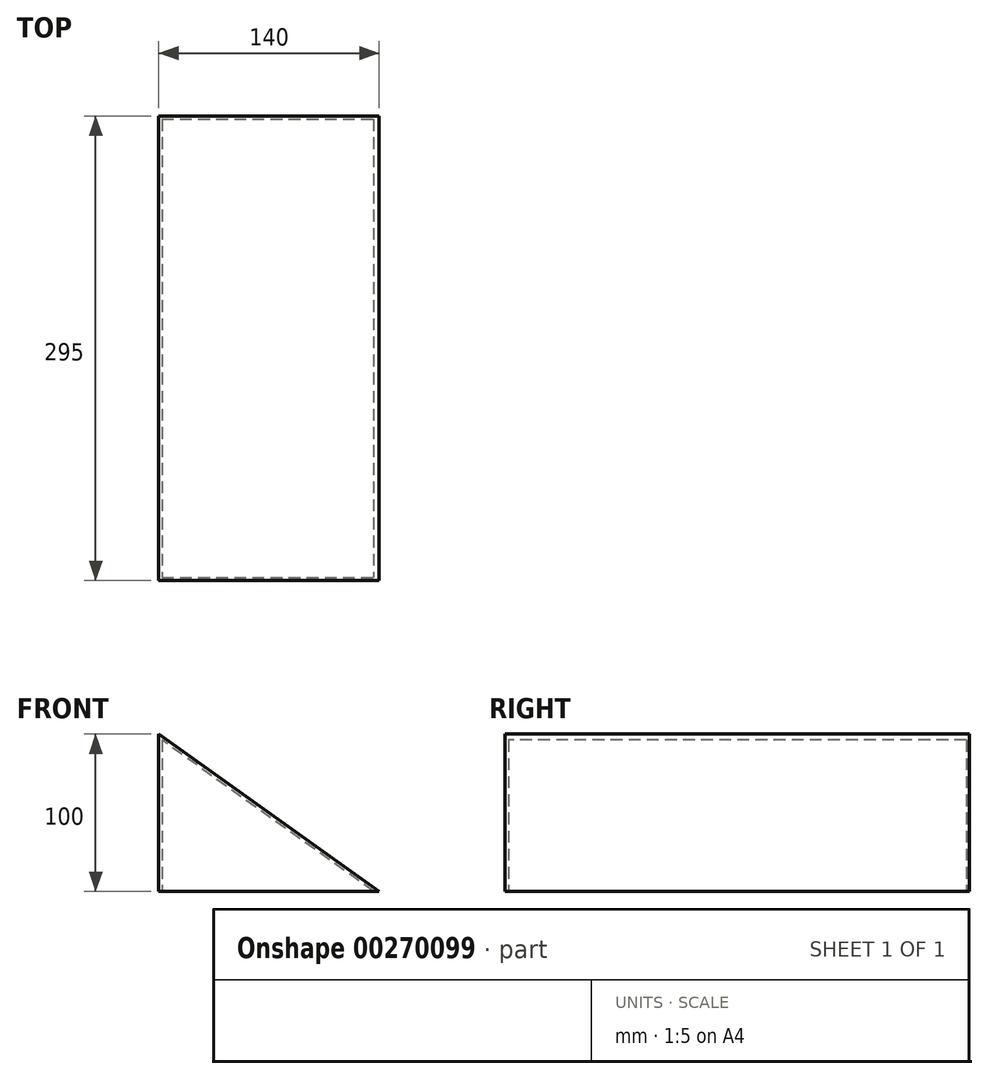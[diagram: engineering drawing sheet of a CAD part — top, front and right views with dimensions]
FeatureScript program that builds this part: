
annotation { "Feature Type Name" : "Feature", "Feature Type Description" : "" }
export const myFeature = defineFeature(function(context is Context, id is Id, definition is map)
    precondition{}
    {
        {
            var Q0;
            Q0=qCreatedBy(makeId("Front.planeOp"),FACE);
            var sketch = newSketch(context, id + "F0", { "sketchPlane" : qUnion([Q0])});
            skLineSegment(sketch, "E0", {"start": v(-70, 0) * mm, "end": v(70, 0) * mm});
            skLineSegment(sketch, "E1", {"start": v(70, 0) * mm, "end": v(-70, 100) * mm});
            skLineSegment(sketch, "E2", {"start": v(-70, 100) * mm, "end": v(-70, 0) * mm});
            skPoint(sketch, "E3", {"position": v(0, 0) * mm});
            skSolve(sketch);
        }
        {
            var Q0;
            Q0=makeQuery(id+"F0.imprint","IMPRINT",FACE,{"disambiguationData":[TD([[makeQuery(id+"F0.imprint","IMPRINT",EDGE,{"derivedFrom":sQuery(id+"F0.wireOp",EDGE,"E0")}),1.0]])]});
            extrude(context, id + "F1", {"entities" : qUnion([Q0]), "oppositeDirection" : true, "depth" : 295 * mm});
        }
        {
            var Q0;
            Q0=makeQuery(id+"F1.opExtrude","SWEPT_FACE",FACE,{"disambiguationData":[OSD([sQuery(id+"F0.wireOp",EDGE,"E0")])]});
            shell(context, id + "F2", {"entities" : qUnion([Q0]), "thickness" : 2 * mm});
        }
    });
